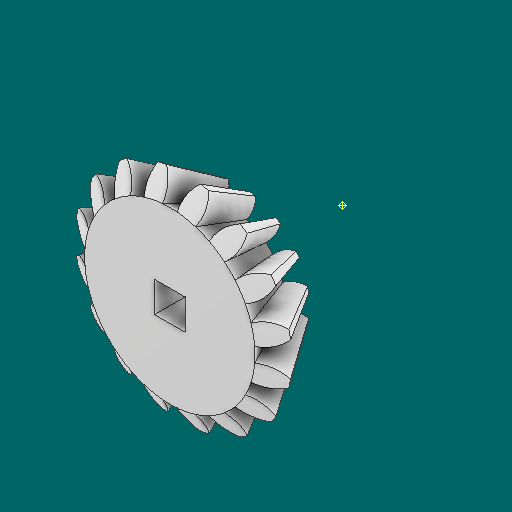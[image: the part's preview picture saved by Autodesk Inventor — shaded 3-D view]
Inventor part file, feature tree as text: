
AUTODESK INVENTOR PART (.ipt)
format: ipt  version: 2023.1 (Build 271208000, 208)  size: 499,200 bytes
history: native  units: in
note: dims shown in document units (in); Inventor stores cm internally (conversion verified against a paired STEP export)
features: other x30, sketch x2
ambient origin geometry x8: Origin, YZ Plane, XZ Plane, XY Plane, X Axis, Y Axis, Z Axis, Center Point
bodies: Solid1 (feature_tree)
feature tree (32):
  other  "Bevel Gear1"
  other  "Solid1::Bevel Gear1"
  other  "TaggingFeature1"
  other  "Teeth Body Sketch"
  other  "Start Sketch"
  other  "End Sketch"
  other  "End Sketch Right"
  other  "End Sketch Left"
  other  "Body Sketch"
  sketch  "Sketch6"  dims[d0=0.3937in]
  sketch  "Sketch8"  dims[d48=0.0in d49=0.0in d50=90.0deg d52=0.0in d53=0.0in d54=0.0in]
  other  "3D Sketch Right"
  other  "3D Sketch Left"
  other  "Mesh Plane"
  other  "Top Plane"
  other  "Mesh Plane2"
  other  "Tooth Plane"
  other  "End Plane"
  other  "End Plane Right"
  other  "End Plane Left"
  other  "Z Axis_1"
  other  "Top Point"
  other  "Start Point"
  other  "End Point"
  other  "Srf1"
  other  "Srf1::Derived"
  other  "Start plane iMate"
  other  "Mesh iMate2"
  other  "Axis Angle iMate"
  other  "Axis iMate"
  other  "Mesh iMate"
  other  "Intersection iMate"
